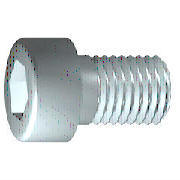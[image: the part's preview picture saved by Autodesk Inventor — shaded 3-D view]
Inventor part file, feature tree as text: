
AUTODESK INVENTOR PART (.ipt)
format: ipt  version: 2020.2 (Build 242310000, 310)  size: 195,584 bytes
history: native  units: mm (DEFAULTED — no unit token found)
features: sketch x2, extrude x1, plane x1, fillet x1
ambient origin geometry x7: Origin, YZ Plane, XY Plane, X Axis, Y Axis, Z Axis, Center Point
bodies: Solid1 (feature_tree), Body (feature_tree)
feature tree (5):
  extrude  "Slot"  Depth=5.0mm
  plane  "Work Plane1"
  fillet  "Fillet2"  Radius=5.0mm
  sketch  "Sketch1"  dims[d1=15.2mm d2=0.49086mm d3=5.0mm]
  sketch  "Sketch2"  dims[d4=2.5mm d5=60.0deg d6=5.0mm d7=5.0mm d8=4.618802mm d9=8.5mm d10=90.0deg d11=10.0mm d12=0.0mm d13=15.2mm d14=0.0mm d15=0.49076mm d16=0.49076mm d17=0.5mm d19=0.0mm d26=16.0mm d27=45.0deg d28=0.0mm d29=0.0mm d30=0.2mm]
